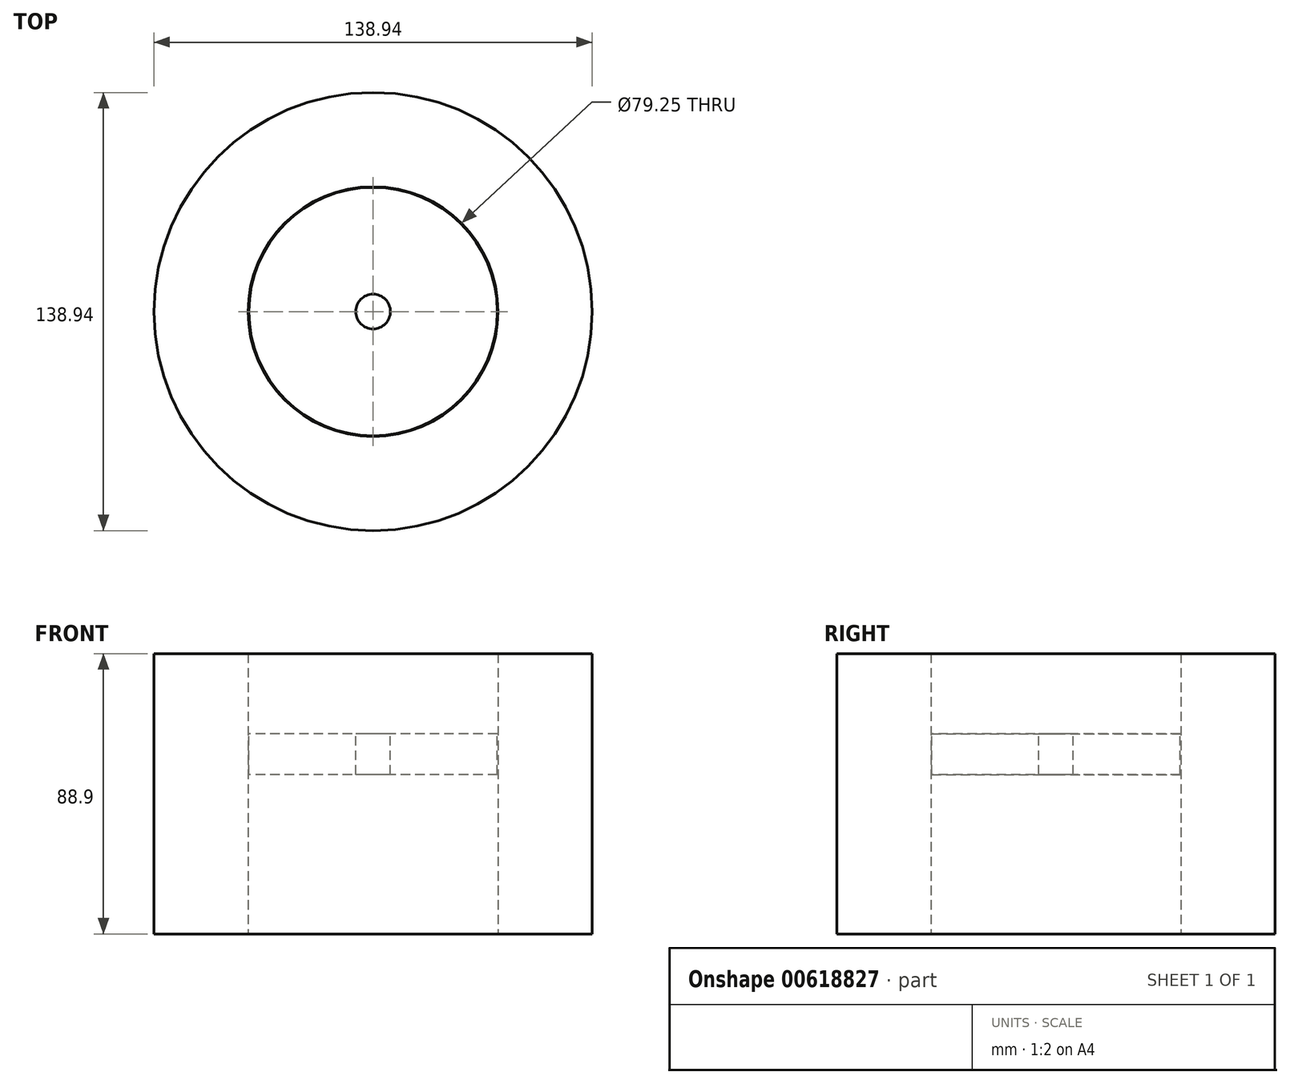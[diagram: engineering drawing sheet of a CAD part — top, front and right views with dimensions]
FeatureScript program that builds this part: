
annotation { "Feature Type Name" : "Feature", "Feature Type Description" : "" }
export const myFeature = defineFeature(function(context is Context, id is Id, definition is map)
    precondition{}
    {
        {
            var Q0;
            Q0=qCreatedBy(makeId("Top.planeOp"),FACE);
            var sketch = newSketch(context, id + "F0", { "sketchPlane" : qUnion([Q0])});
            skCircle(sketch, "E0", {"center": v(0, 0) * mm, "radius": 50.8 * mm});
            skCircle(sketch, "E1", {"center": v(0, 0) * mm, "radius": 39.62 * mm});
            skSolve(sketch);
        }
        {
            var Q0;
            Q0=makeQuery(id+"F0.imprint","IMPRINT",FACE,{"disambiguationData":[TD([[makeQuery(id+"F0.imprint","IMPRINT",EDGE,{"derivedFrom":sQuery(id+"F0.wireOp",EDGE,"E0")}),1.0]])]});
            extrude(context, id + "F1", {"entities" : qUnion([Q0]), "depth" : 88.9 * mm, "offsetDistance" : 25.4 * mm});
        }
        {
            var Q0;
            Q0=makeQuery(id+"F1.opExtrude","CAP_FACE",FACE,{"disambiguationData":[OSD([sQuery(id+"F0.wireOp",EDGE,"E0"),sQuery(id+"F0.wireOp",EDGE,"E1")])],"isStart":false});
            var sketch = newSketch(context, id + "F2", { "sketchPlane" : qUnion([Q0])});
            skCircle(sketch, "E2", {"center": v(0, 0) * mm, "radius": 39.37 * mm});
            skCircle(sketch, "E3", {"center": v(0, 0) * mm, "radius": 5.5 * mm});
            skSolve(sketch);
        }
        {
            var Q0;
            Q0=makeQuery(id+"F2.imprint","IMPRINT",FACE,{"disambiguationData":[TD([[makeQuery(id+"F2.imprint","IMPRINT",EDGE,{"derivedFrom":sQuery(id+"F2.wireOp",EDGE,"E2")}),1.0]])]});
            extrude(context, id + "F3", {"entities" : qUnion([Q0]), "oppositeDirection" : true, "depth" : 38.35 * mm, "offsetDistance" : 25.4 * mm});
        }
        {
            var Q0;
            Q0=makeQuery(id+"F3.opExtrude","CAP_FACE",FACE,{"disambiguationData":[OSD([sQuery(id+"F2.wireOp",EDGE,"E2"),sQuery(id+"F2.wireOp",EDGE,"E3")])],"isStart":true});
            extrude(context, id + "F4", {"entities" : qUnion([Q0]), "operationType" : NewBodyOperationType.REMOVE, "oppositeDirection" : true, "depth" : 25.4 * mm, "offsetDistance" : 25.4 * mm});
        }
        {
            var Q0;
            Q0=makeQuery(id+"F1.opExtrude","CAP_FACE",FACE,{"disambiguationData":[OSD([sQuery(id+"F0.wireOp",EDGE,"E0"),sQuery(id+"F0.wireOp",EDGE,"E1")])],"isStart":false});
            var sketch = newSketch(context, id + "F5", { "sketchPlane" : qUnion([Q0])});
            skCircle(sketch, "E4", {"center": v(0, 0) * mm, "radius": 69.47 * mm});
            skSolve(sketch);
        }
        {
            var Q0;
            Q0=makeQuery(id+"F5.imprint","IMPRINT",FACE,{"disambiguationData":[TD([[makeQuery(id+"F5.imprint","IMPRINT",EDGE,{"derivedFrom":sQuery(id+"F5.wireOp",EDGE,"E4")}),1.0]])]});
            extrude(context, id + "F6", {"entities" : qUnion([Q0]), "operationType" : NewBodyOperationType.ADD, "oppositeDirection" : true, "depth" : 88.9 * mm, "offsetDistance" : 25.4 * mm});
        }
    });
